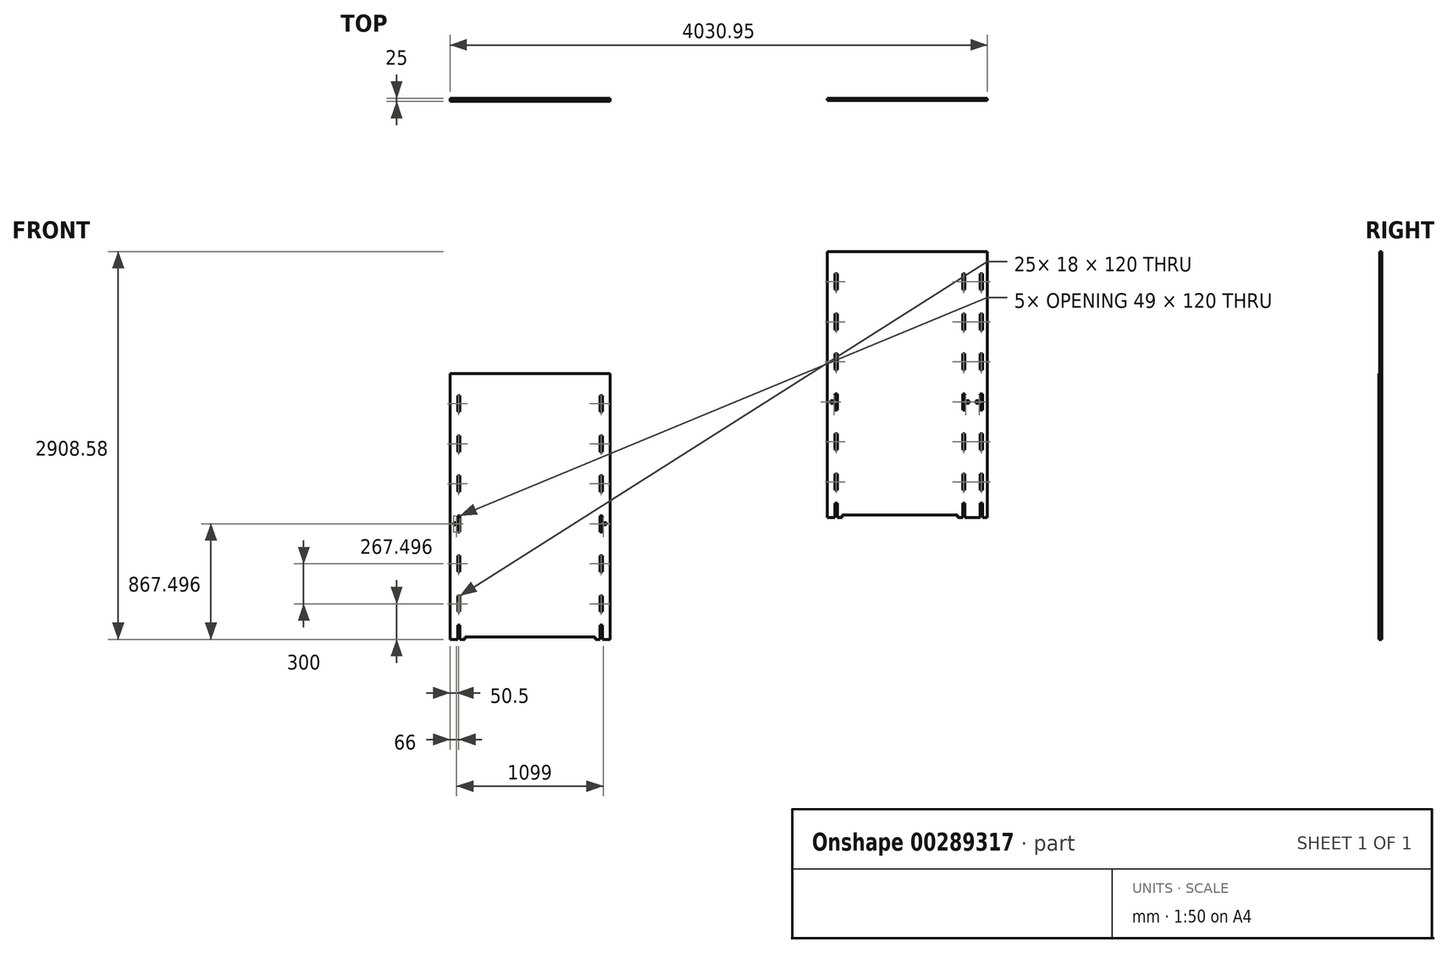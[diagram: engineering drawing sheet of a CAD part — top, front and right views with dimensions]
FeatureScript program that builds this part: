
annotation { "Feature Type Name" : "Feature", "Feature Type Description" : "" }
export const myFeature = defineFeature(function(context is Context, id is Id, definition is map)
    precondition{}
    {
        {
            var Q0;
            Q0=qCreatedBy(makeId("Front.planeOp"),FACE);
            var sketch = newSketch(context, id + "F0", { "sketchPlane" : qUnion([Q0])});
            skLineSegment(sketch, "E0.bottom", {"start": v(-383.5, -202.61) * mm, "end": v(-352.5, -202.61) * mm});
            skLineSegment(sketch, "E0.top", {"start": v(-383.5, -220.61) * mm, "end": v(-352.5, -220.61) * mm});
            skLineSegment(sketch, "E0.left", {"start": v(-383.5, -202.61) * mm, "end": v(-383.5, -220.61) * mm});
            skLineSegment(sketch, "E0.right", {"start": v(-352.5, -202.61) * mm, "end": v(-352.5, -220.61) * mm});
            skLineSegment(sketch, "E1.bottom", {"start": v(-352.5, -151.61) * mm, "end": v(-334.5, -151.61) * mm});
            skLineSegment(sketch, "E1.top", {"start": v(-352.5, -271.61) * mm, "end": v(-334.5, -271.61) * mm});
            skLineSegment(sketch, "E1.left", {"start": v(-352.5, -151.61) * mm, "end": v(-352.5, -271.61) * mm});
            skLineSegment(sketch, "E1.right", {"start": v(-334.5, -151.61) * mm, "end": v(-334.5, -271.61) * mm});
            skLineSegment(sketch, "E2", {"start": v(-334.5, -211.61) * mm, "end": v(190.5, -211.61) * mm});
            skPoint(sketch, "E2.endSnap0", {"position": v(-334.5, -211.61) * mm});
            skLineSegment(sketch, "E3", {"start": v(190.5, -211.61) * mm, "end": v(190.5, -173.59) * mm});
            skLineSegment(sketch, "E4.bottom", {"start": v(-334.5, 28.39) * mm, "end": v(-352.5, 28.39) * mm});
            skLineSegment(sketch, "E4.top", {"start": v(-334.5, 148.39) * mm, "end": v(-352.5, 148.39) * mm});
            skLineSegment(sketch, "E4.left", {"start": v(-334.5, 28.39) * mm, "end": v(-334.5, 148.39) * mm});
            skLineSegment(sketch, "E4.right", {"start": v(-352.5, 28.39) * mm, "end": v(-352.5, 148.39) * mm});
            skLineSegment(sketch, "E5.bottom", {"start": v(-334.5, 328.39) * mm, "end": v(-352.5, 328.39) * mm});
            skLineSegment(sketch, "E5.top", {"start": v(-334.5, 448.39) * mm, "end": v(-352.5, 448.39) * mm});
            skLineSegment(sketch, "E5.left", {"start": v(-334.5, 328.39) * mm, "end": v(-334.5, 448.39) * mm});
            skLineSegment(sketch, "E5.right", {"start": v(-352.5, 328.39) * mm, "end": v(-352.5, 448.39) * mm});
            skLineSegment(sketch, "E6.bottom", {"start": v(-334.5, 628.39) * mm, "end": v(-352.5, 628.39) * mm});
            skLineSegment(sketch, "E6.top", {"start": v(-334.5, 748.39) * mm, "end": v(-352.5, 748.39) * mm});
            skLineSegment(sketch, "E6.left", {"start": v(-334.5, 628.39) * mm, "end": v(-334.5, 748.39) * mm});
            skLineSegment(sketch, "E6.right", {"start": v(-352.5, 628.39) * mm, "end": v(-352.5, 748.39) * mm});
            skLineSegment(sketch, "E7", {"start": v(-334.5, 915.39) * mm, "end": v(-352.5, 915.39) * mm});
            skLineSegment(sketch, "E8", {"start": v(-352.5, 915.39) * mm, "end": v(-409.5, 915.39) * mm});
            skLineSegment(sketch, "E9.bottom", {"start": v(-352.5, -451.61) * mm, "end": v(-334.5, -451.61) * mm});
            skLineSegment(sketch, "E9.top", {"start": v(-352.5, -571.61) * mm, "end": v(-334.5, -571.61) * mm});
            skLineSegment(sketch, "E9.left", {"start": v(-352.5, -451.61) * mm, "end": v(-352.5, -571.61) * mm});
            skLineSegment(sketch, "E9.right", {"start": v(-334.5, -451.61) * mm, "end": v(-334.5, -571.61) * mm});
            skLineSegment(sketch, "E10.bottom", {"start": v(-352.5, -751.61) * mm, "end": v(-334.5, -751.61) * mm});
            skLineSegment(sketch, "E10.top", {"start": v(-352.5, -871.61) * mm, "end": v(-334.5, -871.61) * mm});
            skLineSegment(sketch, "E10.left", {"start": v(-352.5, -751.61) * mm, "end": v(-352.5, -871.61) * mm});
            skLineSegment(sketch, "E10.right", {"start": v(-334.5, -751.61) * mm, "end": v(-334.5, -871.61) * mm});
            skLineSegment(sketch, "E11.bottom", {"start": v(-352.5, -971.61) * mm, "end": v(-334.5, -971.61) * mm});
            skLineSegment(sketch, "E11.left", {"start": v(-352.5, -971.61) * mm, "end": v(-352.5, -1079.11) * mm});
            skLineSegment(sketch, "E11.right", {"start": v(-334.5, -971.61) * mm, "end": v(-334.5, -1079.11) * mm});
            skLineSegment(sketch, "E12", {"start": v(-334.5, -1079.11) * mm, "end": v(-298.5, -1079.11) * mm});
            skLineSegment(sketch, "E13", {"start": v(-298.5, -1079.11) * mm, "end": v(-298.5, -1061.11) * mm});
            skLineSegment(sketch, "E14", {"start": v(-298.5, -1061.11) * mm, "end": v(190.5, -1061.11) * mm});
            skLineSegment(sketch, "E15", {"start": v(-352.5, -1079.11) * mm, "end": v(-409.5, -1079.11) * mm});
            skLineSegment(sketch, "E16", {"start": v(-409.5, 915.39) * mm, "end": v(-409.5, -1079.11) * mm});
            skLineSegment(sketch, "E17.MirrorCS", {"start": v(715.5, -1079.11) * mm, "end": v(679.5, -1079.11) * mm});
            skLineSegment(sketch, "E18.MirrorCS", {"start": v(733.5, -151.61) * mm, "end": v(715.5, -151.61) * mm});
            skLineSegment(sketch, "E19.MirrorCS", {"start": v(764.5, -220.61) * mm, "end": v(733.5, -220.61) * mm});
            skLineSegment(sketch, "E20.MirrorCS", {"start": v(733.5, -971.61) * mm, "end": v(715.5, -971.61) * mm});
            skLineSegment(sketch, "E21.MirrorCS", {"start": v(764.5, -202.61) * mm, "end": v(733.5, -202.61) * mm});
            skLineSegment(sketch, "E22.MirrorCS", {"start": v(733.5, -1079.11) * mm, "end": v(790.5, -1079.11) * mm});
            skLineSegment(sketch, "E23.MirrorCS", {"start": v(733.5, -971.61) * mm, "end": v(733.5, -1079.11) * mm});
            skLineSegment(sketch, "E24.MirrorCS", {"start": v(733.5, -751.61) * mm, "end": v(715.5, -751.61) * mm});
            skLineSegment(sketch, "E25.MirrorCS", {"start": v(733.5, -271.61) * mm, "end": v(715.5, -271.61) * mm});
            skLineSegment(sketch, "E26.MirrorCS", {"start": v(733.5, -202.61) * mm, "end": v(733.5, -220.61) * mm});
            skLineSegment(sketch, "E27.MirrorCS", {"start": v(715.5, -971.61) * mm, "end": v(715.5, -1079.11) * mm});
            skLineSegment(sketch, "E28.MirrorCS", {"start": v(764.5, -202.61) * mm, "end": v(764.5, -220.61) * mm});
            skLineSegment(sketch, "E29.MirrorCS", {"start": v(733.5, -871.61) * mm, "end": v(715.5, -871.61) * mm});
            skLineSegment(sketch, "E30.MirrorCS", {"start": v(679.5, -1079.11) * mm, "end": v(679.5, -1061.11) * mm});
            skLineSegment(sketch, "E31.MirrorCS", {"start": v(733.5, -151.61) * mm, "end": v(733.5, -271.61) * mm});
            skLineSegment(sketch, "E32.MirrorCS", {"start": v(715.5, -151.61) * mm, "end": v(715.5, -271.61) * mm});
            skLineSegment(sketch, "E33.MirrorCS", {"start": v(733.5, -451.61) * mm, "end": v(733.5, -571.61) * mm});
            skLineSegment(sketch, "E34.MirrorCS", {"start": v(733.5, 28.39) * mm, "end": v(733.5, 148.39) * mm});
            skLineSegment(sketch, "E35.MirrorCS", {"start": v(715.5, 328.39) * mm, "end": v(733.5, 328.39) * mm});
            skLineSegment(sketch, "E36.MirrorCS", {"start": v(715.5, 748.39) * mm, "end": v(733.5, 748.39) * mm});
            skLineSegment(sketch, "E37.MirrorCS", {"start": v(715.5, 148.39) * mm, "end": v(733.5, 148.39) * mm});
            skLineSegment(sketch, "E38.MirrorCS", {"start": v(733.5, 915.39) * mm, "end": v(790.5, 915.39) * mm});
            skLineSegment(sketch, "E39.MirrorCS", {"start": v(715.5, 448.39) * mm, "end": v(733.5, 448.39) * mm});
            skLineSegment(sketch, "E40.MirrorCS", {"start": v(733.5, -751.61) * mm, "end": v(733.5, -871.61) * mm});
            skLineSegment(sketch, "E41.MirrorCS", {"start": v(715.5, 28.39) * mm, "end": v(733.5, 28.39) * mm});
            skLineSegment(sketch, "E42.MirrorCS", {"start": v(715.5, 915.39) * mm, "end": v(733.5, 915.39) * mm});
            skLineSegment(sketch, "E43.MirrorCS", {"start": v(715.5, -751.61) * mm, "end": v(715.5, -871.61) * mm});
            skLineSegment(sketch, "E44.MirrorCS", {"start": v(733.5, 328.39) * mm, "end": v(733.5, 448.39) * mm});
            skLineSegment(sketch, "E45.MirrorCS", {"start": v(733.5, -451.61) * mm, "end": v(715.5, -451.61) * mm});
            skLineSegment(sketch, "E46.MirrorCS", {"start": v(733.5, 628.39) * mm, "end": v(733.5, 748.39) * mm});
            skLineSegment(sketch, "E47.MirrorCS", {"start": v(733.5, -571.61) * mm, "end": v(715.5, -571.61) * mm});
            skLineSegment(sketch, "E48.MirrorCS", {"start": v(715.5, 28.39) * mm, "end": v(715.5, 148.39) * mm});
            skLineSegment(sketch, "E49.MirrorCS", {"start": v(715.5, 628.39) * mm, "end": v(733.5, 628.39) * mm});
            skLineSegment(sketch, "E50.MirrorCS", {"start": v(715.5, -451.61) * mm, "end": v(715.5, -571.61) * mm});
            skLineSegment(sketch, "E51.MirrorCS", {"start": v(790.5, 915.39) * mm, "end": v(790.5, -1079.11) * mm});
            skLineSegment(sketch, "E52.MirrorCS", {"start": v(715.5, 628.39) * mm, "end": v(715.5, 748.39) * mm});
            skLineSegment(sketch, "E53.MirrorCS", {"start": v(715.5, 328.39) * mm, "end": v(715.5, 448.39) * mm});
            skLineSegment(sketch, "E54.MirrorCS", {"start": v(679.5, -1061.11) * mm, "end": v(190.5, -1061.11) * mm});
            skLineSegment(sketch, "E55.MirrorCS", {"start": v(715.5, -211.61) * mm, "end": v(190.5, -211.61) * mm});
            skPoint(sketch, "E56.MirrorP", {"position": v(715.5, -211.61) * mm});
            skLineSegment(sketch, "E57", {"start": v(715.5, 915.39) * mm, "end": v(-334.5, 915.39) * mm});
            skSolve(sketch);
        }
        {
            var Q0;
            Q0=qCreatedBy(makeId("Front.planeOp"),FACE);
            var sketch = newSketch(context, id + "F1", { "sketchPlane" : qUnion([Q0])});
            skLineSegment(sketch, "E58.bottom", {"start": v(2447.44, 711.47) * mm, "end": v(2478.44, 711.47) * mm});
            skLineSegment(sketch, "E58.top", {"start": v(2447.44, 693.47) * mm, "end": v(2478.44, 693.47) * mm});
            skLineSegment(sketch, "E58.right", {"start": v(2478.44, 711.47) * mm, "end": v(2478.44, 693.47) * mm});
            skLineSegment(sketch, "E59.bottom", {"start": v(2478.44, 762.47) * mm, "end": v(2496.44, 762.47) * mm});
            skLineSegment(sketch, "E59.top", {"start": v(2478.44, 642.47) * mm, "end": v(2496.44, 642.47) * mm});
            skLineSegment(sketch, "E59.left", {"start": v(2478.44, 762.47) * mm, "end": v(2478.44, 642.47) * mm});
            skLineSegment(sketch, "E59.right", {"start": v(2496.44, 762.47) * mm, "end": v(2496.44, 642.47) * mm});
            skPoint(sketch, "E60.endSnap0", {"position": v(2496.44, 702.47) * mm});
            skLineSegment(sketch, "E61.bottom", {"start": v(2496.44, 942.47) * mm, "end": v(2478.44, 942.47) * mm});
            skLineSegment(sketch, "E61.top", {"start": v(2496.44, 1062.47) * mm, "end": v(2478.44, 1062.47) * mm});
            skLineSegment(sketch, "E61.left", {"start": v(2496.44, 942.47) * mm, "end": v(2496.44, 1062.47) * mm});
            skLineSegment(sketch, "E61.right", {"start": v(2478.44, 942.47) * mm, "end": v(2478.44, 1062.47) * mm});
            skLineSegment(sketch, "E62.bottom", {"start": v(2496.44, 1242.47) * mm, "end": v(2478.44, 1242.47) * mm});
            skLineSegment(sketch, "E62.top", {"start": v(2496.44, 1362.47) * mm, "end": v(2478.44, 1362.47) * mm});
            skLineSegment(sketch, "E62.left", {"start": v(2496.44, 1242.47) * mm, "end": v(2496.44, 1362.47) * mm});
            skLineSegment(sketch, "E62.right", {"start": v(2478.44, 1242.47) * mm, "end": v(2478.44, 1362.47) * mm});
            skLineSegment(sketch, "E63.bottom", {"start": v(2496.44, 1542.47) * mm, "end": v(2478.44, 1542.47) * mm});
            skLineSegment(sketch, "E63.top", {"start": v(2496.44, 1662.47) * mm, "end": v(2478.44, 1662.47) * mm});
            skLineSegment(sketch, "E63.left", {"start": v(2496.44, 1542.47) * mm, "end": v(2496.44, 1662.47) * mm});
            skLineSegment(sketch, "E63.right", {"start": v(2478.44, 1542.47) * mm, "end": v(2478.44, 1662.47) * mm});
            skLineSegment(sketch, "E64.bottom", {"start": v(2478.44, 462.47) * mm, "end": v(2496.44, 462.47) * mm});
            skLineSegment(sketch, "E64.top", {"start": v(2478.44, 342.47) * mm, "end": v(2496.44, 342.47) * mm});
            skLineSegment(sketch, "E64.left", {"start": v(2478.44, 462.47) * mm, "end": v(2478.44, 342.47) * mm});
            skLineSegment(sketch, "E64.right", {"start": v(2496.44, 462.47) * mm, "end": v(2496.44, 342.47) * mm});
            skLineSegment(sketch, "E65.bottom", {"start": v(2478.44, 162.47) * mm, "end": v(2496.44, 162.47) * mm});
            skLineSegment(sketch, "E65.top", {"start": v(2478.44, 42.47) * mm, "end": v(2496.44, 42.47) * mm});
            skLineSegment(sketch, "E65.left", {"start": v(2478.44, 162.47) * mm, "end": v(2478.44, 42.47) * mm});
            skLineSegment(sketch, "E65.right", {"start": v(2496.44, 162.47) * mm, "end": v(2496.44, 42.47) * mm});
            skLineSegment(sketch, "E66.bottom", {"start": v(2478.44, -57.53) * mm, "end": v(2496.44, -57.53) * mm});
            skLineSegment(sketch, "E66.left", {"start": v(2478.44, -57.53) * mm, "end": v(2478.44, -165.03) * mm});
            skLineSegment(sketch, "E66.right", {"start": v(2496.44, -57.53) * mm, "end": v(2496.44, -165.03) * mm});
            skLineSegment(sketch, "E67", {"start": v(2447.44, 711.47) * mm, "end": v(2447.44, 693.47) * mm});
            skLineSegment(sketch, "E68", {"start": v(2496.44, -165.03) * mm, "end": v(2532.44, -165.03) * mm});
            skLineSegment(sketch, "E69", {"start": v(2532.44, -165.03) * mm, "end": v(2532.44, -147.03) * mm});
            skLineSegment(sketch, "E70", {"start": v(2532.44, -147.03) * mm, "end": v(2965.94, -147.03) * mm});
            skLineSegment(sketch, "E71", {"start": v(2478.44, -165.03) * mm, "end": v(2421.44, -165.03) * mm});
            skLineSegment(sketch, "E72", {"start": v(2496.44, 1829.47) * mm, "end": v(2478.44, 1829.47) * mm});
            skLineSegment(sketch, "E73", {"start": v(2478.44, 1829.47) * mm, "end": v(2421.44, 1829.47) * mm});
            skLineSegment(sketch, "E74", {"start": v(2421.44, 1829.47) * mm, "end": v(2421.44, -165.03) * mm});
            skLineSegment(sketch, "E75", {"start": v(2965.94, -147.03) * mm, "end": v(2965.94, -90.61) * mm});
            skLineSegment(sketch, "E76.MirrorCS", {"start": v(3435.44, 1829.47) * mm, "end": v(3453.44, 1829.47) * mm});
            skLineSegment(sketch, "E77.MirrorCS", {"start": v(3435.44, 1662.47) * mm, "end": v(3453.44, 1662.47) * mm});
            skLineSegment(sketch, "E78.MirrorCS", {"start": v(3453.44, 1542.47) * mm, "end": v(3453.44, 1662.47) * mm});
            skLineSegment(sketch, "E79.MirrorCS", {"start": v(3435.44, 1542.47) * mm, "end": v(3453.44, 1542.47) * mm});
            skLineSegment(sketch, "E80.MirrorCS", {"start": v(3435.44, 1542.47) * mm, "end": v(3435.44, 1662.47) * mm});
            skLineSegment(sketch, "E81.MirrorCS", {"start": v(3435.44, 942.47) * mm, "end": v(3453.44, 942.47) * mm});
            skLineSegment(sketch, "E82.MirrorCS", {"start": v(3435.44, 1242.47) * mm, "end": v(3453.44, 1242.47) * mm});
            skLineSegment(sketch, "E83.MirrorCS", {"start": v(3435.44, 1062.47) * mm, "end": v(3453.44, 1062.47) * mm});
            skLineSegment(sketch, "E84.MirrorCS", {"start": v(3435.44, 1362.47) * mm, "end": v(3453.44, 1362.47) * mm});
            skLineSegment(sketch, "E85.MirrorCS", {"start": v(3453.44, 1242.47) * mm, "end": v(3453.44, 1362.47) * mm});
            skLineSegment(sketch, "E86.MirrorCS", {"start": v(3435.44, 942.47) * mm, "end": v(3435.44, 1062.47) * mm});
            skLineSegment(sketch, "E87.MirrorCS", {"start": v(3453.44, 942.47) * mm, "end": v(3453.44, 1062.47) * mm});
            skLineSegment(sketch, "E88.MirrorCS", {"start": v(3435.44, 1242.47) * mm, "end": v(3435.44, 1362.47) * mm});
            skLineSegment(sketch, "E89.MirrorCS", {"start": v(3453.44, 642.47) * mm, "end": v(3435.44, 642.47) * mm});
            skLineSegment(sketch, "E90.MirrorCS", {"start": v(3453.44, 711.47) * mm, "end": v(3453.44, 693.47) * mm});
            skLineSegment(sketch, "E91.MirrorCS", {"start": v(3453.44, 762.47) * mm, "end": v(3435.44, 762.47) * mm});
            skLineSegment(sketch, "E92.MirrorCS", {"start": v(3453.44, 762.47) * mm, "end": v(3453.44, 642.47) * mm});
            skLineSegment(sketch, "E93.MirrorCS", {"start": v(3453.44, 342.47) * mm, "end": v(3435.44, 342.47) * mm});
            skLineSegment(sketch, "E94.MirrorCS", {"start": v(3435.44, 762.47) * mm, "end": v(3435.44, 642.47) * mm});
            skLineSegment(sketch, "E95.MirrorCS", {"start": v(3453.44, 462.47) * mm, "end": v(3435.44, 462.47) * mm});
            skLineSegment(sketch, "E96.MirrorCS", {"start": v(3435.44, 462.47) * mm, "end": v(3435.44, 342.47) * mm});
            skPoint(sketch, "E97.MirrorP", {"position": v(3435.44, 702.47) * mm});
            skLineSegment(sketch, "E98.MirrorCS", {"start": v(3453.44, 462.47) * mm, "end": v(3453.44, 342.47) * mm});
            skLineSegment(sketch, "E99.MirrorCS", {"start": v(3484.44, 711.47) * mm, "end": v(3453.44, 711.47) * mm});
            skLineSegment(sketch, "E100.MirrorCS", {"start": v(3484.44, 711.47) * mm, "end": v(3484.44, 693.47) * mm});
            skLineSegment(sketch, "E101.MirrorCS", {"start": v(3484.44, 693.47) * mm, "end": v(3453.44, 693.47) * mm});
            skLineSegment(sketch, "E102.MirrorCS", {"start": v(3453.44, 162.47) * mm, "end": v(3435.44, 162.47) * mm});
            skLineSegment(sketch, "E103.MirrorCS", {"start": v(3435.44, -165.03) * mm, "end": v(3399.44, -165.03) * mm});
            skLineSegment(sketch, "E104.MirrorCS", {"start": v(3453.44, 42.47) * mm, "end": v(3435.44, 42.47) * mm});
            skLineSegment(sketch, "E105.MirrorCS", {"start": v(3453.44, -57.53) * mm, "end": v(3435.44, -57.53) * mm});
            skLineSegment(sketch, "E106.MirrorCS", {"start": v(3399.44, -165.03) * mm, "end": v(3399.44, -147.03) * mm});
            skLineSegment(sketch, "E107.MirrorCS", {"start": v(3399.44, -147.03) * mm, "end": v(2965.94, -147.03) * mm});
            skLineSegment(sketch, "E108.MirrorCS", {"start": v(3453.44, 162.47) * mm, "end": v(3453.44, 42.47) * mm});
            skLineSegment(sketch, "E109.MirrorCS", {"start": v(3435.44, 162.47) * mm, "end": v(3435.44, 42.47) * mm});
            skLineSegment(sketch, "E110.MirrorCS", {"start": v(3435.44, -57.53) * mm, "end": v(3435.44, -165.03) * mm});
            skLineSegment(sketch, "E111.MirrorCS", {"start": v(3453.44, -57.53) * mm, "end": v(3453.44, -165.03) * mm});
            skLineSegment(sketch, "E112", {"start": v(3453.44, -165.03) * mm, "end": v(3510.44, -165.03) * mm});
            skLineSegment(sketch, "E113", {"start": v(3510.44, -165.03) * mm, "end": v(3510.44, -105.27) * mm});
            skLineSegment(sketch, "E114.MirrorCS", {"start": v(3567.44, 462.47) * mm, "end": v(3585.44, 462.47) * mm});
            skLineSegment(sketch, "E115.MirrorCS", {"start": v(3567.44, 342.47) * mm, "end": v(3585.44, 342.47) * mm});
            skLineSegment(sketch, "E116.MirrorCS", {"start": v(3585.44, 1542.47) * mm, "end": v(3567.44, 1542.47) * mm});
            skLineSegment(sketch, "E117.MirrorCS", {"start": v(3585.44, 1242.47) * mm, "end": v(3567.44, 1242.47) * mm});
            skLineSegment(sketch, "E118.MirrorCS", {"start": v(3567.44, 642.47) * mm, "end": v(3585.44, 642.47) * mm});
            skLineSegment(sketch, "E119.MirrorCS", {"start": v(3567.44, 42.47) * mm, "end": v(3585.44, 42.47) * mm});
            skLineSegment(sketch, "E120.MirrorCS", {"start": v(3585.44, 1362.47) * mm, "end": v(3567.44, 1362.47) * mm});
            skLineSegment(sketch, "E121.MirrorCS", {"start": v(3567.44, 711.47) * mm, "end": v(3567.44, 693.47) * mm});
            skLineSegment(sketch, "E122.MirrorCS", {"start": v(3567.44, -57.53) * mm, "end": v(3585.44, -57.53) * mm});
            skLineSegment(sketch, "E123.MirrorCS", {"start": v(3567.44, 762.47) * mm, "end": v(3585.44, 762.47) * mm});
            skLineSegment(sketch, "E124.MirrorCS", {"start": v(3585.44, 1062.47) * mm, "end": v(3567.44, 1062.47) * mm});
            skLineSegment(sketch, "E125.MirrorCS", {"start": v(3567.44, 162.47) * mm, "end": v(3585.44, 162.47) * mm});
            skLineSegment(sketch, "E126.MirrorCS", {"start": v(3585.44, 1662.47) * mm, "end": v(3567.44, 1662.47) * mm});
            skLineSegment(sketch, "E127.MirrorCS", {"start": v(3585.44, -165.03) * mm, "end": v(3621.44, -165.03) * mm});
            skLineSegment(sketch, "E128.MirrorCS", {"start": v(3621.44, -165.03) * mm, "end": v(3621.44, -147.03) * mm});
            skLineSegment(sketch, "E129.MirrorCS", {"start": v(3585.44, 942.47) * mm, "end": v(3567.44, 942.47) * mm});
            skLineSegment(sketch, "E130.MirrorCS", {"start": v(3567.44, 462.47) * mm, "end": v(3567.44, 342.47) * mm});
            skLineSegment(sketch, "E131.MirrorCS", {"start": v(3585.44, 762.47) * mm, "end": v(3585.44, 642.47) * mm});
            skLineSegment(sketch, "E132.MirrorCS", {"start": v(3567.44, 762.47) * mm, "end": v(3567.44, 642.47) * mm});
            skLineSegment(sketch, "E133.MirrorCS", {"start": v(3585.44, 1829.47) * mm, "end": v(3567.44, 1829.47) * mm});
            skLineSegment(sketch, "E134.MirrorCS", {"start": v(3585.44, 462.47) * mm, "end": v(3585.44, 342.47) * mm});
            skLineSegment(sketch, "E135.MirrorCS", {"start": v(3585.44, 162.47) * mm, "end": v(3585.44, 42.47) * mm});
            skLineSegment(sketch, "E136.MirrorCS", {"start": v(3585.44, 1542.47) * mm, "end": v(3585.44, 1662.47) * mm});
            skLineSegment(sketch, "E137.MirrorCS", {"start": v(3585.44, 1242.47) * mm, "end": v(3585.44, 1362.47) * mm});
            skPoint(sketch, "E138.MirrorP", {"position": v(3585.44, 702.47) * mm});
            skLineSegment(sketch, "E139.MirrorCS", {"start": v(3585.44, -57.53) * mm, "end": v(3585.44, -165.03) * mm});
            skLineSegment(sketch, "E140.MirrorCS", {"start": v(3567.44, -57.53) * mm, "end": v(3567.44, -165.03) * mm});
            skLineSegment(sketch, "E141.MirrorCS", {"start": v(3567.44, 1542.47) * mm, "end": v(3567.44, 1662.47) * mm});
            skLineSegment(sketch, "E142.MirrorCS", {"start": v(3567.44, 1242.47) * mm, "end": v(3567.44, 1362.47) * mm});
            skLineSegment(sketch, "E143.MirrorCS", {"start": v(3567.44, 162.47) * mm, "end": v(3567.44, 42.47) * mm});
            skLineSegment(sketch, "E144.MirrorCS", {"start": v(3567.44, 942.47) * mm, "end": v(3567.44, 1062.47) * mm});
            skLineSegment(sketch, "E145.MirrorCS", {"start": v(3585.44, 942.47) * mm, "end": v(3585.44, 1062.47) * mm});
            skLineSegment(sketch, "E146.MirrorCS", {"start": v(3536.44, 711.47) * mm, "end": v(3536.44, 693.47) * mm});
            skLineSegment(sketch, "E147.MirrorCS", {"start": v(3536.44, 693.47) * mm, "end": v(3567.44, 693.47) * mm});
            skLineSegment(sketch, "E148.MirrorCS", {"start": v(3536.44, 711.47) * mm, "end": v(3567.44, 711.47) * mm});
            skLineSegment(sketch, "E149", {"start": v(3585.44, 1829.47) * mm, "end": v(3621.44, 1829.47) * mm});
            skLineSegment(sketch, "E150", {"start": v(3621.44, 1829.47) * mm, "end": v(3621.44, -147.03) * mm});
            skLineSegment(sketch, "E151", {"start": v(3567.44, -165.03) * mm, "end": v(3510.44, -165.03) * mm});
            skLineSegment(sketch, "E152", {"start": v(2421.44, 1829.47) * mm, "end": v(3621.44, 1829.47) * mm});
            skSolve(sketch);
        }
        {
            var Q0;
            {var subQ9=sQuery(id+"F0.wireOp",EDGE,"E0.bottom");Q0=makeQuery(id+"F0.imprint","IMPRINT",FACE,{"disambiguationData":[TD([[makeQuery(id+"F0.imprint","IMPRINT",EDGE,{"derivedFrom":subQ9}),1.0]])]});}
            extrude(context, id + "F2", {"entities" : qUnion([Q0]), "depth" : 25 * mm});
        }
        {
            var Q0;
            {var subQ9=sQuery(id+"F1.wireOp",EDGE,"E58.bottom");Q0=makeQuery(id+"F1.imprint","IMPRINT",FACE,{"disambiguationData":[TD([[makeQuery(id+"F1.imprint","IMPRINT",EDGE,{"derivedFrom":subQ9}),1.0]])]});}
            extrude(context, id + "F3", {"entities" : qUnion([Q0]), "depth" : 18 * mm});
        }
    });
